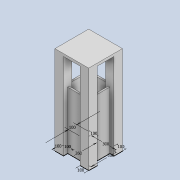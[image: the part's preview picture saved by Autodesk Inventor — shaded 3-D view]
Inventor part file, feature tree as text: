
AUTODESK INVENTOR PART (.ipt)
format: ipt  version: 2021 (Build 250183000, 183)  size: 142,848 bytes
history: native  units: mm
features: extrude x4, sketch x2
ambient origin geometry x8: Origin, YZ Plane, XZ Plane, XY Plane, X Axis, Y Axis, Z Axis, Center Point
bodies: Solid1 (feature_tree)
feature tree (6):
  sketch  "Sketch1"  dims[d0=300.0mm d1=300.0mm]
  extrude  "Extrusion1"  Depth=300.0mm
  extrude  "Extrusion2"  Depth=100.0mm
  extrude  "Extrusion3"  Depth=100.0mm
  extrude  "Extrusion4"  Depth=100.0mm
  sketch  "Sketch2"  dims[d2=100.0mm d3=100.0mm d4=100.0mm d5=100.0mm d6=100.0mm d7=100.0mm d8=1050.0mm d9=0.0mm d10=680.0mm d11=0.0mm d12=30.0mm d13=0.0mm d14=260.0mm d15=10.0mm d16=0.0mm]
